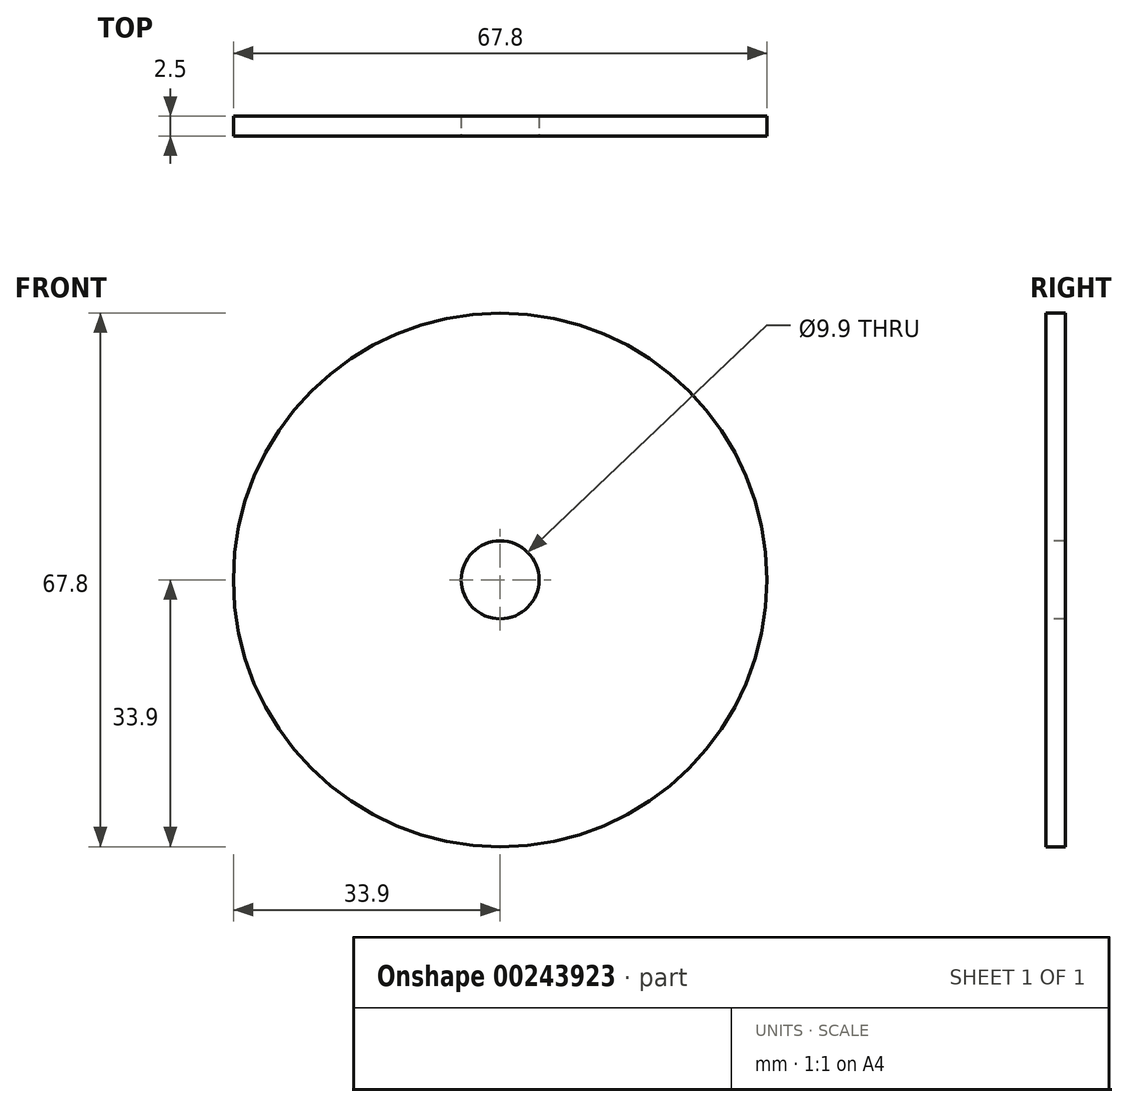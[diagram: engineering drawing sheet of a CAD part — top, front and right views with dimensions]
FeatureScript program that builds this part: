
annotation { "Feature Type Name" : "Feature", "Feature Type Description" : "" }
export const myFeature = defineFeature(function(context is Context, id is Id, definition is map)
    precondition{}
    {
        {
            var Q0;
            Q0=qCreatedBy(makeId("Front.planeOp"),FACE);
            var sketch = newSketch(context, id + "F0", { "sketchPlane" : qUnion([Q0])});
            skCircle(sketch, "E0", {"center": v(0, 0) * mm, "radius": 33.9 * mm});
            skSolve(sketch);
        }
        {
            var Q0;
            Q0=makeQuery(id+"F0.imprint","IMPRINT",FACE,{"disambiguationData":[TD([[makeQuery(id+"F0.imprint","IMPRINT",EDGE,{"derivedFrom":sQuery(id+"F0.wireOp",EDGE,"E0")}),1.0]])]});
            extrude(context, id + "F1", {"entities" : qUnion([Q0]), "depth" : 2.5 * mm, "offsetDistance" : 25 * mm});
        }
        {
            var Q0;
            Q0=makeQuery(id+"F1.opExtrude","CAP_FACE",FACE,{"disambiguationData":[OSD([sQuery(id+"F0.wireOp",EDGE,"E0")])],"isStart":false});
            var sketch = newSketch(context, id + "F2", { "sketchPlane" : qUnion([Q0])});
            skCircle(sketch, "E1", {"center": v(0, 0) * mm, "radius": 4.95 * mm});
            skSolve(sketch);
        }
        {
            var Q0;
            Q0=makeQuery(id+"F2.imprint","IMPRINT",FACE,{"disambiguationData":[TD([[makeQuery(id+"F2.imprint","IMPRINT",EDGE,{"derivedFrom":sQuery(id+"F2.wireOp",EDGE,"E1")}),1.0]])]});
            extrude(context, id + "F3", {"entities" : qUnion([Q0]), "operationType" : NewBodyOperationType.REMOVE, "oppositeDirection" : true, "depth" : 30 * mm, "offsetDistance" : 25 * mm});
        }
    });
